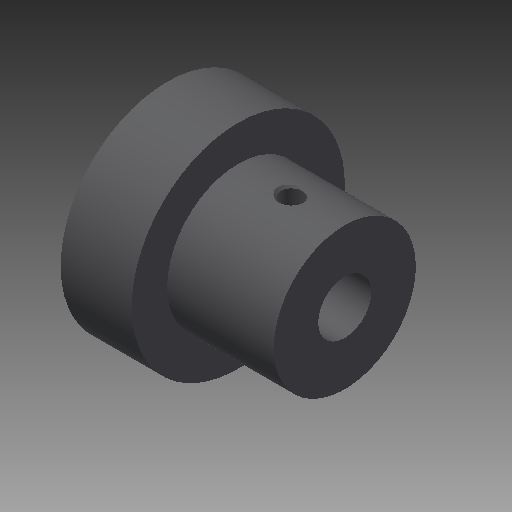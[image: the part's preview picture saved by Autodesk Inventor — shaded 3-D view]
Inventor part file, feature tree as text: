
AUTODESK INVENTOR PART (.ipt)
format: ipt  version: 2019 (Build 230136000, 136)  size: 138,752 bytes
history: native  units: mm
features: other x7, revolve x3, sketch x3, thread x1
ambient origin geometry x8: Origin, YZ Plane, XZ Plane, XY Plane, X Axis, Y Axis, Z Axis, Center Point
bodies: Solid1 (feature_tree)
feature tree (14):
  revolve  "Revolution1"  Angle=360.0deg
  revolve  "Revolution2"  [1 undecoded]
  revolve  "Revolution3"  [1 undecoded]
  thread  "Thread1"  [1 undecoded]
  other  "c_k_XY"
  other  "c_k_YZ"
  other  "c_k_ZX"
  other  "c_k_X"
  other  "c_k_Y"
  other  "c_k_Z"
  other  "c_k_Center"
  sketch  "Sketch_2"  dims[d0=360.0deg d1=360.0deg]
  sketch  "Sketch_4"  dims[d2=360.0deg d3=4.7295mm d4=0.0mm]
  sketch  "Sketch_5"
note: 3 required parameter values undecoded (feature->parameter linkage not recoverable at this tier; creation-order binding heuristic only, values carry confidence <= 0.55)